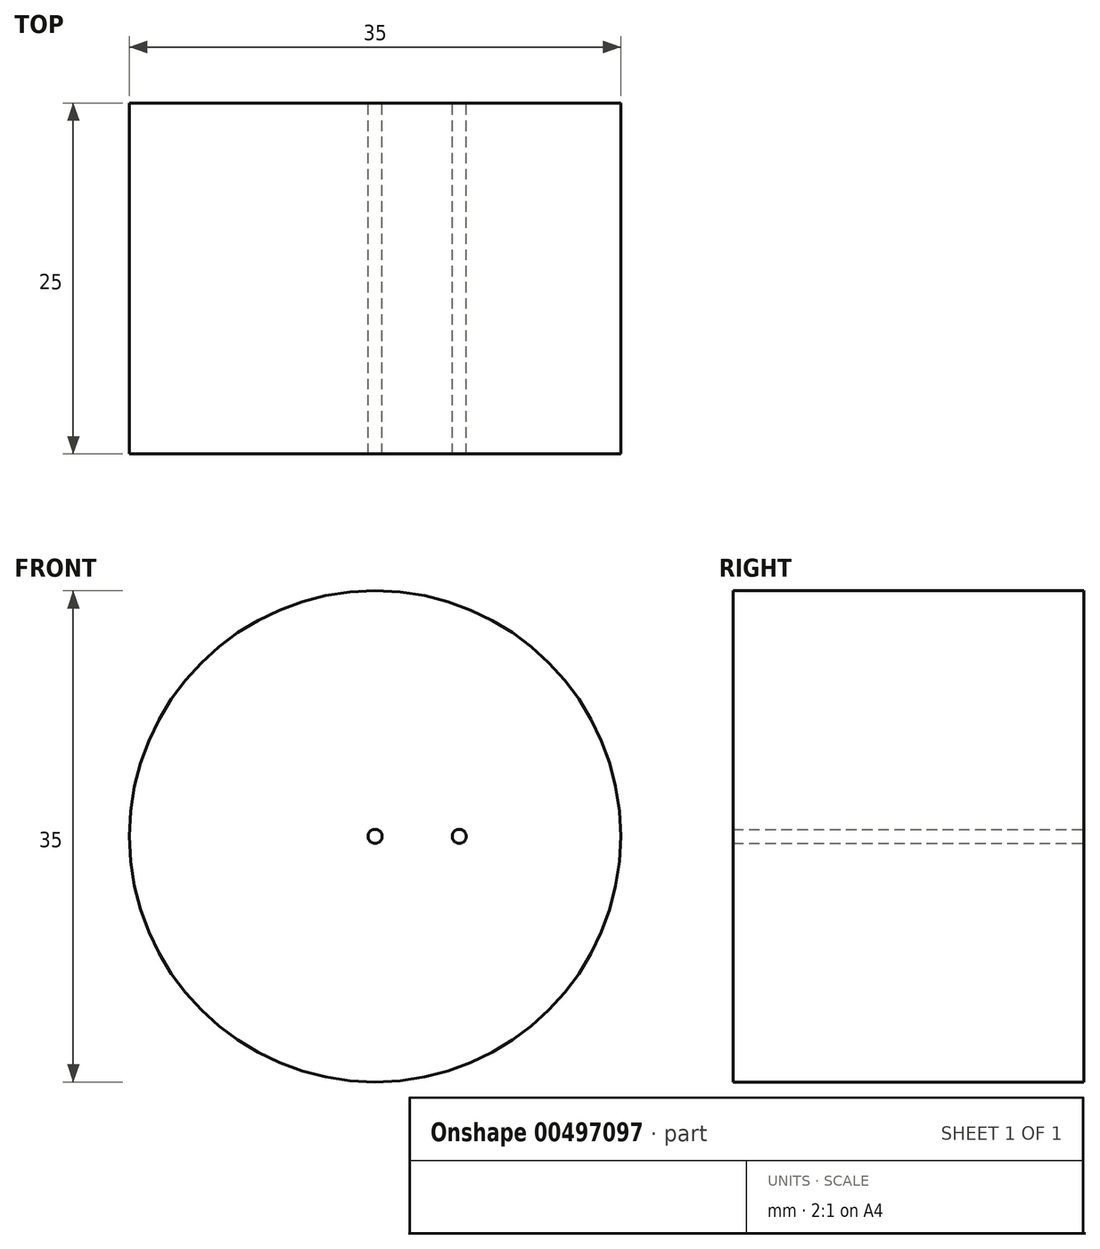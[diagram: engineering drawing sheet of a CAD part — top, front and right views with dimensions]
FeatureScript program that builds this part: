
annotation { "Feature Type Name" : "Feature", "Feature Type Description" : "" }
export const myFeature = defineFeature(function(context is Context, id is Id, definition is map)
    precondition{}
    {
        {
            var Q0;
            Q0=qCreatedBy(makeId("Front.planeOp"),FACE);
            var sketch = newSketch(context, id + "F0", { "sketchPlane" : qUnion([Q0])});
            skCircle(sketch, "E0", {"center": v(0, 0) * mm, "radius": 17.5 * mm});
            skCircle(sketch, "E1", {"center": v(0, 0) * mm, "radius": 0.5 * mm});
            skCircle(sketch, "E2", {"center": v(6, 0) * mm, "radius": 0.5 * mm});
            skLineSegment(sketch, "E3", {"start": v(-0.25, 17.5) * mm, "end": v(-0.25, 0.43) * mm});
            skLineSegment(sketch, "E4", {"start": v(0.25, -17.5) * mm, "end": v(0.25, -0.43) * mm});
            skLineSegment(sketch, "E5", {"start": v(-0.25, 0) * mm, "end": v(0.25, 0) * mm});
            skLineSegment(sketch, "E6.trimOffspring", {"start": v(-0.25, 0) * mm, "end": v(-0.25, -17.5) * mm});
            skLineSegment(sketch, "E7.trimOffspring", {"start": v(0.25, 0.43) * mm, "end": v(0.25, 17.5) * mm});
            skLineSegment(sketch, "E8", {"start": v(5.75, -16.53) * mm, "end": v(5.75, 0) * mm});
            skLineSegment(sketch, "E9", {"start": v(6.25, 16.35) * mm, "end": v(6.25, 0.43) * mm});
            skLineSegment(sketch, "E10", {"start": v(5.75, 0) * mm, "end": v(6, 0) * mm});
            skLineSegment(sketch, "E11.trimOffspring", {"start": v(6.25, 0) * mm, "end": v(6.25, -16.35) * mm});
            skLineSegment(sketch, "E12.trimOffspring", {"start": v(5.75, 0.43) * mm, "end": v(5.75, 16.53) * mm});
            skSolve(sketch);
        }
        {
            var Q0;
            {var subQ0=sQuery(id+"F0.wireOp",EDGE,"E3");Q0=makeQuery(id+"F0.imprint","IMPRINT",FACE,{"disambiguationData":[TD([[makeQuery(id+"F0.imprint","IMPRINT",EDGE,{"derivedFrom":subQ0}),-1.0]])]});}
            var Q1;
            {var subQ4=sQuery(id+"F0.wireOp",EDGE,"E4");Q1=makeQuery(id+"F0.imprint","IMPRINT",FACE,{"disambiguationData":[TD([[makeQuery(id+"F0.imprint","IMPRINT",EDGE,{"derivedFrom":subQ4}),-1.0]])]});}
            var Q2;
            {var subQ0=sQuery(id+"F0.wireOp",EDGE,"E3");Q2=makeQuery(id+"F0.imprint","IMPRINT",FACE,{"disambiguationData":[TD([[makeQuery(id+"F0.imprint","IMPRINT",EDGE,{"derivedFrom":subQ0}),1.0]])]});}
            var Q3;
            {var subQ0=sQuery(id+"F0.wireOp",EDGE,"E4");Q3=makeQuery(id+"F0.imprint","IMPRINT",FACE,{"disambiguationData":[TD([[makeQuery(id+"F0.imprint","IMPRINT",EDGE,{"derivedFrom":subQ0}),1.0]])]});}
            var Q4;
            {var subQ0=sQuery(id+"F0.wireOp",EDGE,"E8");var subQ1=sQuery(id+"F0.wireOp",EDGE,"E0");var subQ2=makeQuery(id+"F0.imprint","INTERSECT",VERTEX,{"derivedFrom":[subQ1,subQ0]});Q4=makeQuery(id+"F0.imprint","IMPRINT",FACE,{"disambiguationData":[TD([[makeQuery(id+"F0.imprint","IMPRINT",EDGE,{"disambiguationData":[TD([[subQ2,-1.0]])],"derivedFrom":subQ1}),1.0]])]});}
            var Q5;
            {var subQ0=sQuery(id+"F0.wireOp",EDGE,"E9");Q5=makeQuery(id+"F0.imprint","IMPRINT",FACE,{"disambiguationData":[TD([[makeQuery(id+"F0.imprint","IMPRINT",EDGE,{"derivedFrom":subQ0}),-1.0]])]});}
            var Q6;
            {var subQ0=sQuery(id+"F0.wireOp",EDGE,"E9");Q6=makeQuery(id+"F0.imprint","IMPRINT",FACE,{"disambiguationData":[TD([[makeQuery(id+"F0.imprint","IMPRINT",EDGE,{"derivedFrom":subQ0}),1.0]])]});}
            extrude(context, id + "F1", {"entities" : qUnion([Q0, Q1, Q2, Q3, Q4, Q5, Q6]), "depth" : 25 * mm, "offsetDistance" : 25 * mm});
        }
    });
